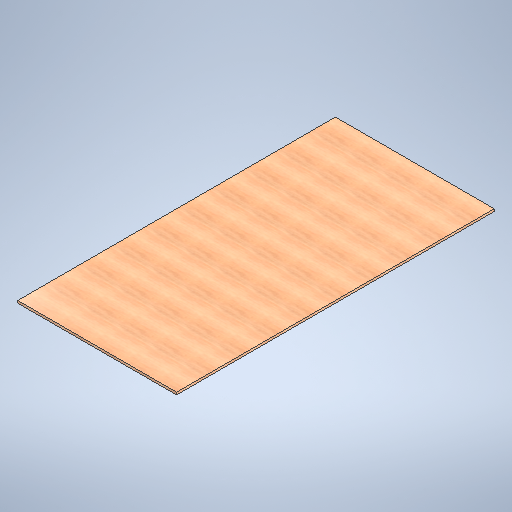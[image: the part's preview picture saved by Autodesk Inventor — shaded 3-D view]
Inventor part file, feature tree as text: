
AUTODESK INVENTOR PART (.ipt)
format: ipt  version: 2025 (Build 290162010, 162A)  size: 315,904 bytes
history: native  units: in
note: dims shown in document units (in); Inventor stores cm internally (conversion verified against a paired STEP export)
features: extrude x1, sketch x1
ambient origin geometry x8: Origin, YZ Plane, XZ Plane, XY Plane, X Axis, Y Axis, Z Axis, Center Point
bodies: Solid1 (feature_tree)
feature tree (2):
  extrude  "Extrusion1"  Depth=48.0in
  sketch  "Sketch1"  dims[d2=96.0in d3=48.0in d4=0.7188in d5=0.0in]
